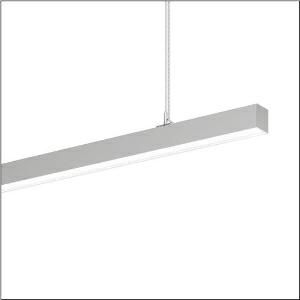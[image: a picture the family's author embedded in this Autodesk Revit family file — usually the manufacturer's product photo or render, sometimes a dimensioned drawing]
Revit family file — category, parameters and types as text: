
# Revit family: silica_r__21_51mx30da34sb_350b
name_source: partatom
category: Lighting Fixtures
units: mm (PartAtom-declared; Revit-internal decimal feet)

## family parameters
Cut with Voids When Loaded = No
Host = Face
Light Source = No
Part Type = Normal
Room Calculation Point = No
Round Connector Dimension = Use Diameter
Shared = No

## types (1)
- --- (1 x LED, 4210 lm, 27.7 W, 3000K)
    Apparent Load = 28 VA
    CIE Flux Codes = 47 79 96 57 100
    Color Rendering = 80
    Color Temperature = 3000K
    Default Elevation = 1800 mm
    Description = Silica® 21, office luminaire, primary optical cover: cover, of PMMA, opal, light emission: direct/indirect distribution, primary light characteristic: symmetric, installation type: suspended mounting, LED, rated luminous flux: 4.210lm, luminous efficacy: 152lm/W, light colour: 830, colour temperature: 3000K, with terminal, 3+2-pole, max. 2.5mm², mains connection: 220..240V, AC, 50/60Hz, rated input power: 27.7W, luminaire housing, of aluminium, metallic grey (RAL 9006), length: 1.204mm, width: 53mm, height: 53mm, protection rating (complete): IP20, insulation class (complete): insulation class I (protective earthing), certification: CE, permissible operating ambient temperature: 0..+35°C, standard: EN 50419, packaging unit: 1 piece
    Height = 53 mm
    Lamp = 1 x LED
    Lamp Light Flux = 4210 lm
    Lamp Power = 27.7 W
    Lamp count = 1
    Length = 1204 mm
    Luminous efficacy = 152 lm/W
    Manufacturer = Siteco
    ModVariant = No
    Model = 51MX30DA34SB
    Mounting Place = Ceiling
    Mounting Type = Pendant
    Number of Poles = 1
    OnlyDefault = Yes
    Power Factor = 1
    Product Name = Silica® 21
    Product group = office luminaire | ceiling pendant
    ProductGroupID = 902
    Protection Class = Protection class I
    Protection Degree = IP 20
    RLX_Detail_Level = 1
    RLX_Emergency_Light_Flux = 0 lm
    RLX_Emergency_Type = 0
    RLX_Emergency_Type_DB = No
    RlxData = <blob elided: 23305 chars, md5=c43af575>
    Socket = socket
    Standby Power = 0 W
    System Light Flux = 4210 lm
    System Power = 28 W
    Type Comments = factory setting: luminous flux: 100 % | dim-lin: 254 | 233 mA
    Type Image = l_1335864.jpg
    URL = http://relux.com
    VarID = @adj_085993
    Voltage = 0 V
    Weight = 0.00 kg
    Width = 53 mm

## geometry (parser evidence)
native form markers: Blend x4, Sweep x13
no freeform markers — native parametric forms only
